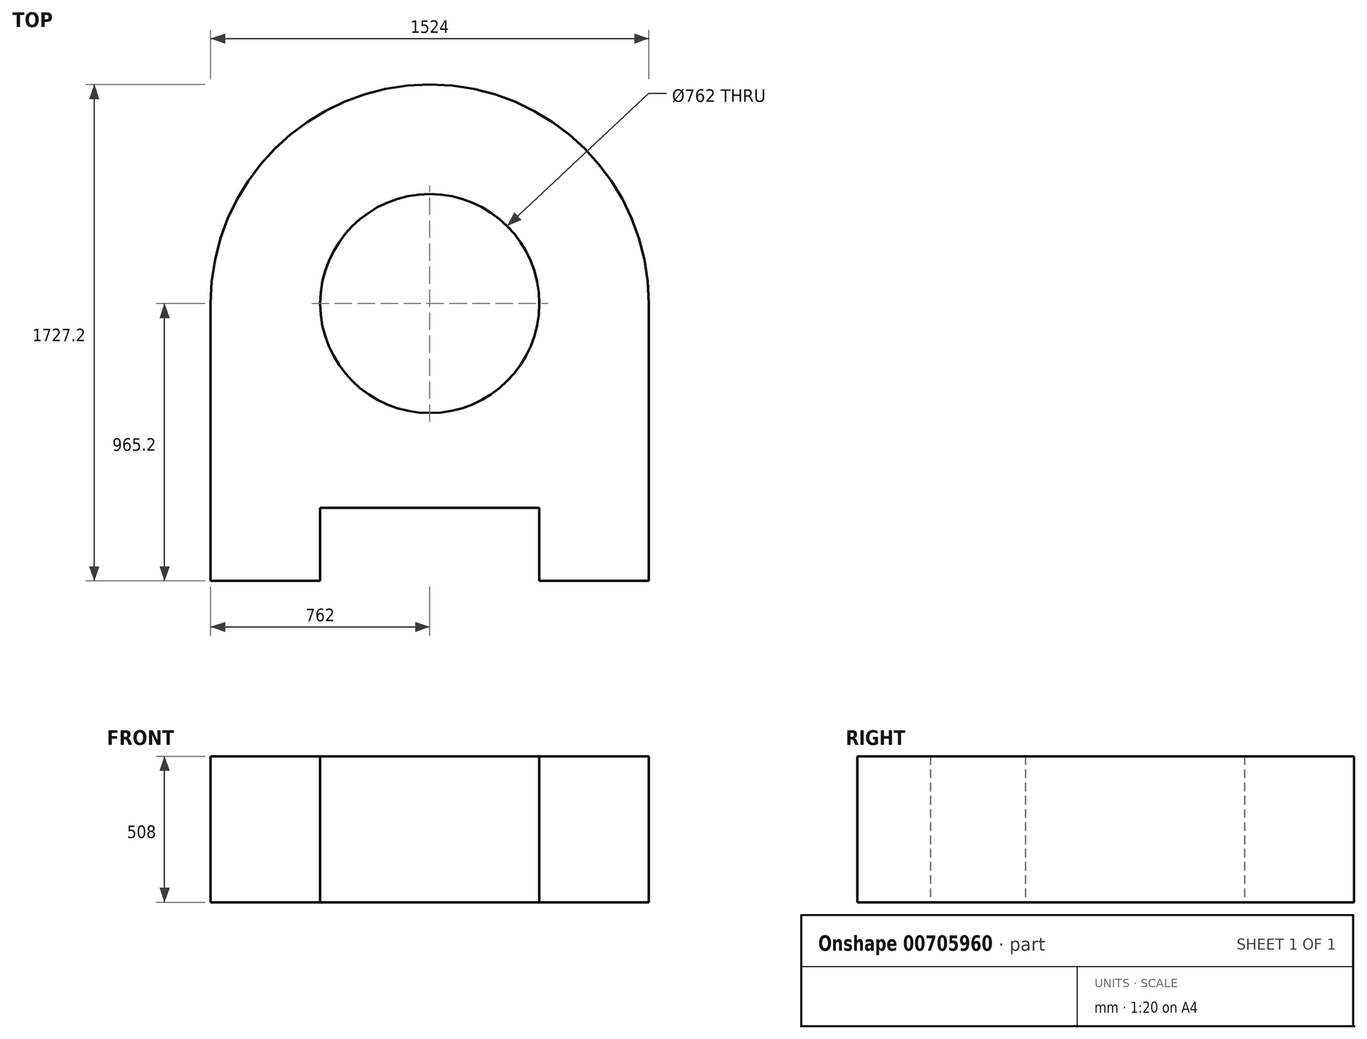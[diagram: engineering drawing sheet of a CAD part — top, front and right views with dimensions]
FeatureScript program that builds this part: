
annotation { "Feature Type Name" : "Feature", "Feature Type Description" : "" }
export const myFeature = defineFeature(function(context is Context, id is Id, definition is map)
    precondition{}
    {
        {
            var Q0;
            Q0=qCreatedBy(makeId("Top.planeOp"),FACE);
            var sketch = newSketch(context, id + "F0", { "sketchPlane" : qUnion([Q0])});
            skLineSegment(sketch, "E0", {"start": v(-381, 0) * mm, "end": v(381, 0) * mm});
            skLineSegment(sketch, "E1", {"start": v(-381, 0) * mm, "end": v(-381, -254) * mm});
            skLineSegment(sketch, "E2", {"start": v(381, 0) * mm, "end": v(381, -254) * mm});
            skLineSegment(sketch, "E3", {"start": v(381, -254) * mm, "end": v(762, -254) * mm});
            skLineSegment(sketch, "E4", {"start": v(-381, -254) * mm, "end": v(-762, -254) * mm});
            skLineSegment(sketch, "E5", {"start": v(-762, -254) * mm, "end": v(-762, 711.2) * mm});
            skLineSegment(sketch, "E6", {"start": v(762, -254) * mm, "end": v(762, 711.2) * mm});
            skArc(sketch, "E7", {"start": v(762, 711.2) * mm, "mid": v(0, 1473.2) * mm, "end": v(-762, 711.2) * mm});
            skCircle(sketch, "E8", {"center": v(0, 711.2) * mm, "radius": 381 * mm});
            skSolve(sketch);
        }
        {
            var Q0;
            Q0 = qSketchRegion(id + "F0", true);
            extrude(context, id + "F1", {"entities" : qUnion([Q0]), "depth" : 508 * mm, "offsetDistance" : 25.4 * mm});
        }
    });
